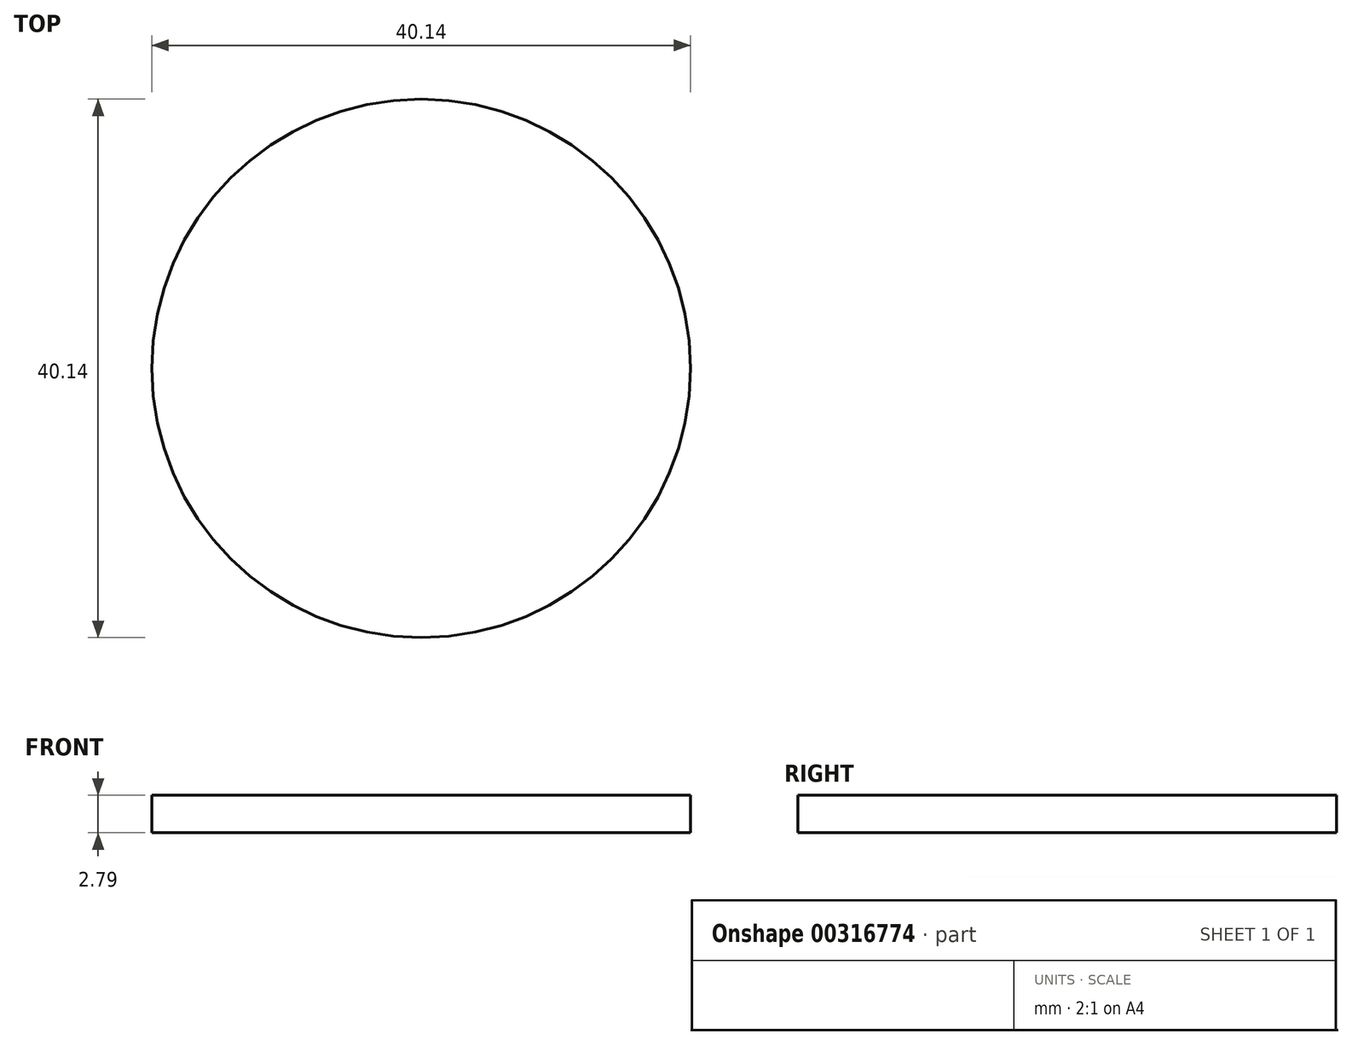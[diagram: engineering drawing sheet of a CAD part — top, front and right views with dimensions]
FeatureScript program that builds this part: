
annotation { "Feature Type Name" : "Feature", "Feature Type Description" : "" }
export const myFeature = defineFeature(function(context is Context, id is Id, definition is map)
    precondition{}
    {
        {
            var Q0;
            Q0=qCreatedBy(makeId("Top.planeOp"),FACE);
            var sketch = newSketch(context, id + "F0", { "sketchPlane" : qUnion([Q0])});
            skCircle(sketch, "E0", {"center": v(0, 0) * mm, "radius": 20.07 * mm});
            skSolve(sketch);
        }
        {
            var Q0;
            Q0 = qSketchRegion(id + "F0", true);
            extrude(context, id + "F1", {"entities" : qUnion([Q0]), "depth" : 2.8 * mm});
        }
    });
